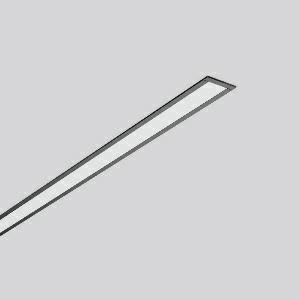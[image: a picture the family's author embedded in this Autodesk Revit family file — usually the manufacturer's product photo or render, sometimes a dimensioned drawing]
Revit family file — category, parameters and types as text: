
# Revit family: less_is_more_27_312176_003_1_03a4
name_source: partatom
category: Lighting Fixtures
units: mm (PartAtom-declared; Revit-internal decimal feet)

## family parameters
Cut with Voids When Loaded = No
Host = Face
Light Source = No
Part Type = Normal
Room Calculation Point = No
Round Connector Dimension = Use Diameter
Shared = No

## types (1)
- LESS IS MORE 27 (1 x LED Modul 840, 1600 lm, 4000)
    Apparent Load = 25 VA
    CIE Flux Codes = 48 79 96 100 100
    Color Rendering = 80
    Color Temperature = 4000
    Default Elevation = 1800 mm
    Description = Series: LESS IS MORE 27
Recessed ceiling and wall luminaire with slim design. Housing: extruded aluminium profile, powder-coated. End cap aluminium powder-coated. Diffuser made of non-yellowing plastic (PMMA), opal. Suitable for Recessed ceiling mounting, wall (recessed). External driver with connecting cable. 
Colour: deep black, matt (RAL 9005)
Length: 1014 mm
Width: 38 mm
Height: 2 mm
Cut-out length: 1006 mm
Cut-out width: 30 mm
Recess height: 45-60 mm
Luminaire: recess height: 37 mm
Lamp: LED
Socket: without socket
Colour temperature: 4000K
Colour rendering index (CRI): 82
System power: 25 W
Rated luminous flux: 1600 lm
Luminous efficiency: 64 lm/W
Control gear: Regulated power supply
Protection class: II
Type of protection: IP 20
    Height = 0 mm  [stored 0 ft]
    Lamp = 1 x LED Modul 840
    Lamp Light Flux = 1600 lm
    Lamp count = 1
    Length = 1014 mm
    Lifetime = 50000 h
    Luminous efficacy = 64 lm/W
    Manufacturer = RZB
    ModVariant = No
    Model = 312176.003.1
    Mounting Place = Ceiling, Wall
    Mounting Type = Recessed
    Number of Poles = 1
    OnlyDefault = Yes
    Power Factor = 1
    Product Name = LESS IS MORE 27
    Product group = Recessed LED linear luminaires
    ProductGroupID = 407
    Protection Class = Protection class II
    Protection Degree = IP 20
    RLX_Detail_Level = 1
    RLX_Emergency_Light_Flux = 0 lm
    RLX_Emergency_Type = 0
    RLX_Emergency_Type_DB = No
    RlxData = <blob elided: 26149 chars, md5=0532a53d>
    Socket = socket
    Standby Power = 0 W
    System Light Flux = 1600 lm
    System Power = 25 W
    Type Comments = Product without accessories
    Type Image = 312176.003.jpg
    URL = http://relux.com
    VarID = ---
    Voltage = 230 V
    Voltage Range = 220-240 V
    Weight = 0.00 kg
    Width = 38 mm

note: [stored X ft] marks values corroborated as IEEE doubles in the binary element streams (Revit-internal decimal feet)

## geometry (parser evidence)
native form markers: Blend x4, Sweep x12
no freeform markers — native parametric forms only
